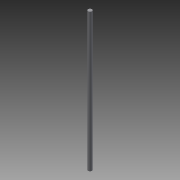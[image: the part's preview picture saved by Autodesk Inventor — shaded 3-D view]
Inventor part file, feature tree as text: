
AUTODESK INVENTOR PART (.ipt)
format: ipt  version: 2013 (Build 170138000, 138)  size: 60,416 bytes
history: native  units: mm
features: extrude x1, sketch x1
ambient origin geometry x8: Origin, YZ Plane, XZ Plane, XY Plane, X Axis, Y Axis, Z Axis, Center Point
bodies: Solid1 (feature_tree)
feature tree (2):
  extrude  "Extrusion1"  Depth=290.0mm TaperAngle=0.0deg
  sketch  "Sketch1"  dims[d0=8.0mm d2=290.0mm d3=0.0mm]
